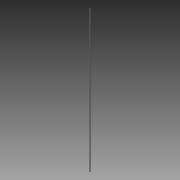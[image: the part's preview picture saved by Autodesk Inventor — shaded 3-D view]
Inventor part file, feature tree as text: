
AUTODESK INVENTOR PART (.ipt)
format: ipt  version: 2015 (Build 190159000, 159)  size: 62,464 bytes
history: native  units: in
note: dims shown in document units (in); Inventor stores cm internally (conversion verified against a paired STEP export)
features: extrude x1, sketch x1
ambient origin geometry x8: Origin, YZ Plane, XZ Plane, XY Plane, X Axis, Y Axis, Z Axis, Center Point
bodies: Solid1 (feature_tree)
feature tree (2):
  extrude  "Extrusion1"  Depth=36.0in TaperAngle=0.0deg
  sketch  "Sketch1"  dims[d0=0.25in d1=36.0in d2=0.0in]
